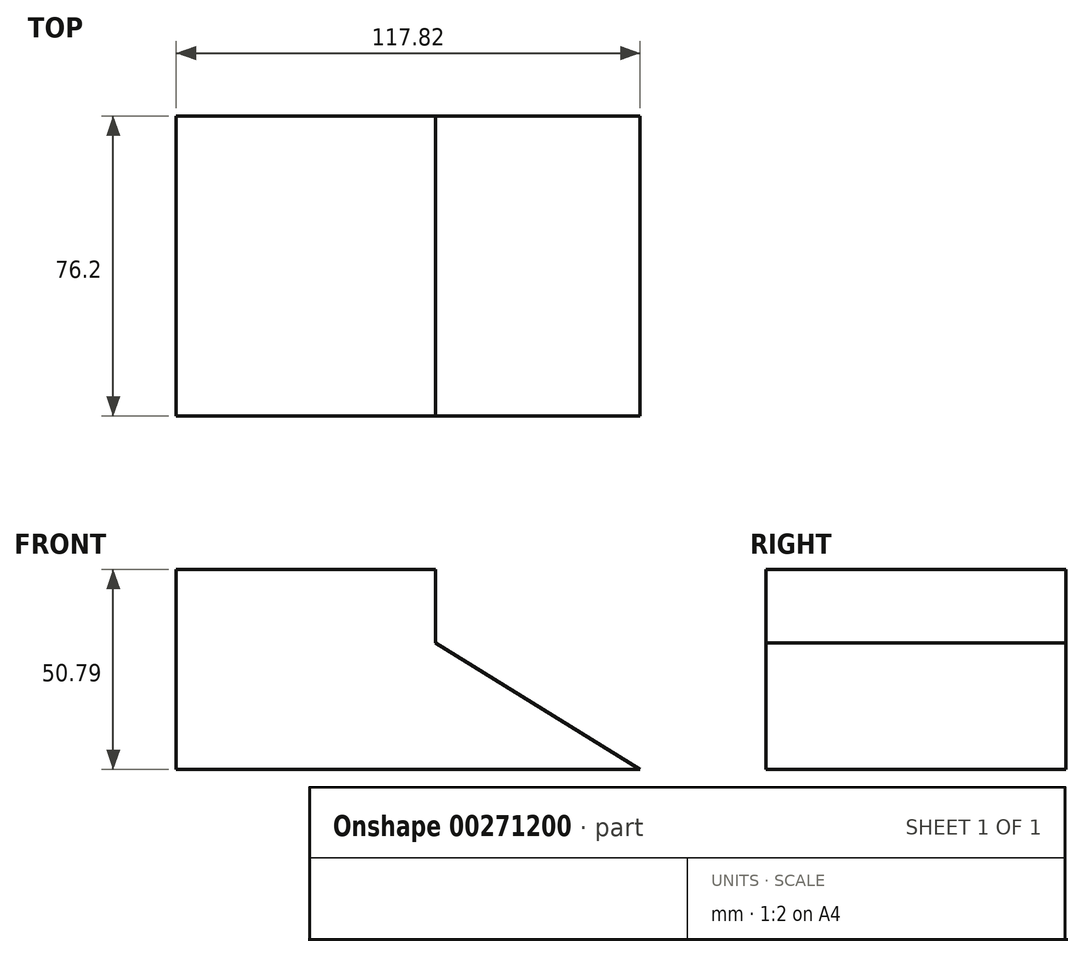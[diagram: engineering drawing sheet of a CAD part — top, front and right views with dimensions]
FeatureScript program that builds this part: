
annotation { "Feature Type Name" : "Feature", "Feature Type Description" : "" }
export const myFeature = defineFeature(function(context is Context, id is Id, definition is map)
    precondition{}
    {
        {
            var Q0;
            Q0=qCreatedBy(makeId("Front.planeOp"),FACE);
            var sketch = newSketch(context, id + "F0", { "sketchPlane" : qUnion([Q0])});
            skLineSegment(sketch, "E0.bottom", {"start": v(0, 0) * mm, "end": v(-65.88, 0) * mm});
            skLineSegment(sketch, "E0.top", {"start": v(0, 50.8) * mm, "end": v(-65.88, 50.8) * mm});
            skLineSegment(sketch, "E0.left", {"start": v(0, 0) * mm, "end": v(0, 50.8) * mm});
            skLineSegment(sketch, "E0.right", {"start": v(-65.88, 0) * mm, "end": v(-65.88, 50.8) * mm});
            skLineSegment(sketch, "E1", {"start": v(0, 32.08) * mm, "end": v(51.94, 0) * mm});
            skLineSegment(sketch, "E2", {"start": v(51.94, 0) * mm, "end": v(-2.1, 0) * mm});
            skSolve(sketch);
        }
        {
            var Q0;
            Q0 = qSketchRegion(id + "F0", true);
            extrude(context, id + "F1", {"entities" : qUnion([Q0]), "depth" : 76.2 * mm});
        }
    });
